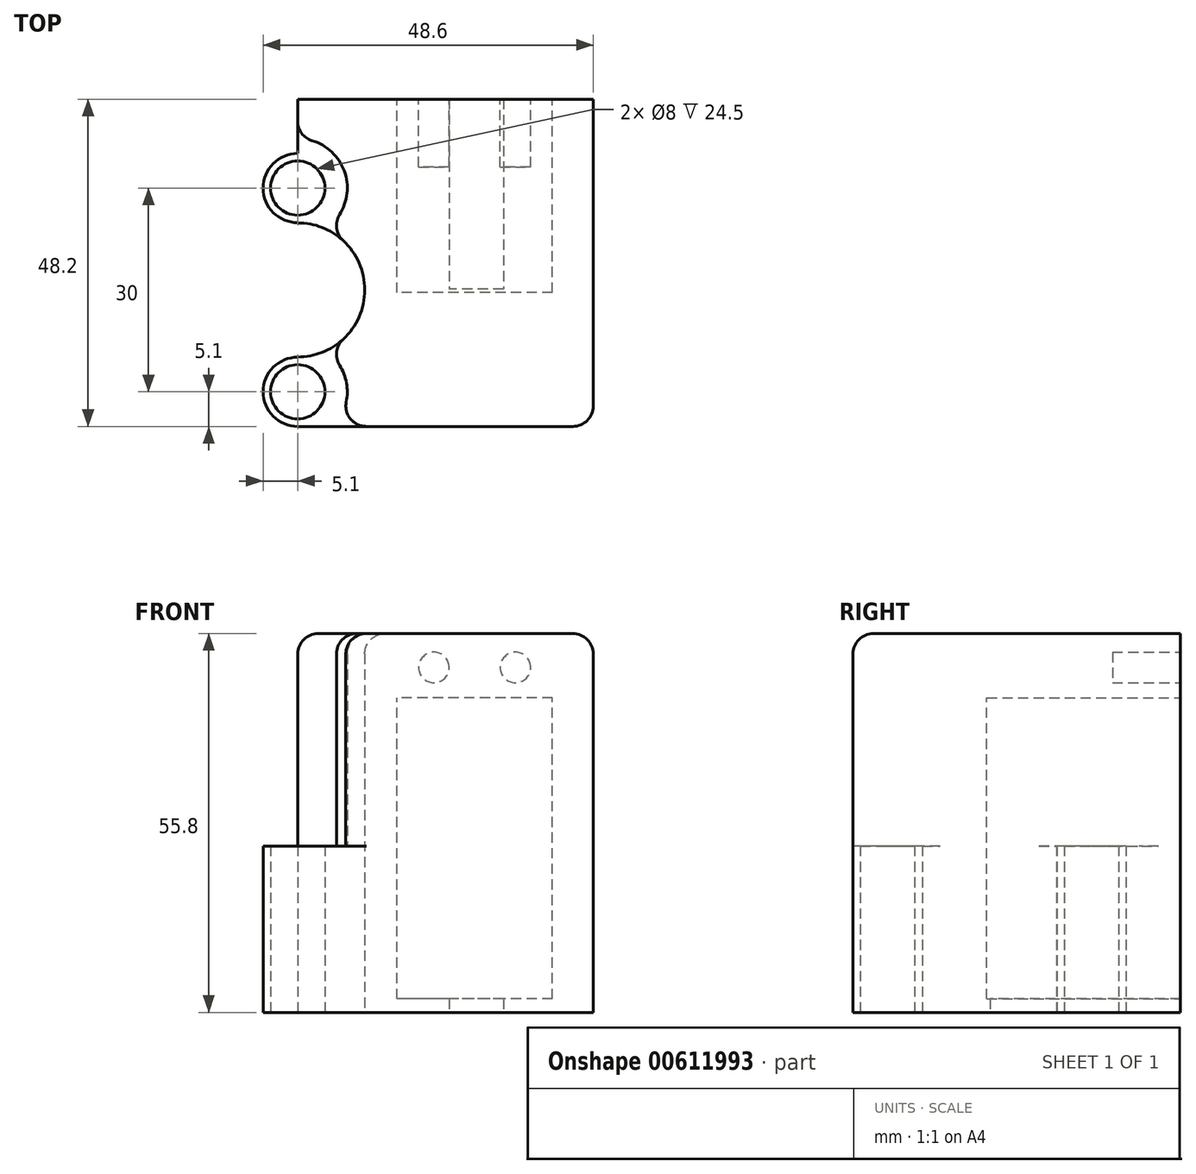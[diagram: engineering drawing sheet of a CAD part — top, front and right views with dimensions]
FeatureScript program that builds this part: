
annotation { "Feature Type Name" : "Feature", "Feature Type Description" : "" }
export const myFeature = defineFeature(function(context is Context, id is Id, definition is map)
    precondition{}
    {
        {
            assignVariable(context, id + "F0", {"name" : "bolt_length", "anyValue" : 24.5});
        }
        {
            assignVariable(context, id + "F1", {"name" : "servo_padding", "anyValue" : 6});
        }
        {
            assignVariable(context, id + "F2", {"name" : "servo_length", "anyValue" : 43.8});
        }
        {
            assignVariable(context, id + "F3", {"name" : "servo_height", "anyValue" : 28});
        }
        {
            assignVariable(context, id + "F4", {"name" : "servo_kerf", "anyValue" : .5});
        }
        {
            var Q0;
            Q0=qCreatedBy(makeId("Top.planeOp"),FACE);
            var sketch = newSketch(context, id + "F5", { "sketchPlane" : qUnion([Q0])});
            skLineSegment(sketch, "E0.bottom", {"start": v(8, -15) * mm, "end": v(-8, -15) * mm, "construction": true});
            skLineSegment(sketch, "E0.top", {"start": v(8, 15) * mm, "end": v(-8, 15) * mm, "construction": true});
            skLineSegment(sketch, "E0.left", {"start": v(8, -15) * mm, "end": v(8, 15) * mm, "construction": true});
            skLineSegment(sketch, "E0.right", {"start": v(-8, -15) * mm, "end": v(-8, 15) * mm, "construction": true});
            skPoint(sketch, "E0.middle", {"position": v(0, 0) * mm});
            skCircle(sketch, "E1", {"center": v(8, 15) * mm, "radius": 4 * mm});
            skCircle(sketch, "E2", {"center": v(8, -15) * mm, "radius": 4 * mm});
            skCircle(sketch, "E3", {"center": v(8, 15) * mm, "radius": 5.1 * mm});
            skCircle(sketch, "E4", {"center": v(8, -15) * mm, "radius": 5.1 * mm});
            skLineSegment(sketch, "E5.bottom", {"start": v(8, 15) * mm, "end": v(51.5, 15) * mm});
            skLineSegment(sketch, "E5.top", {"start": v(8, -15) * mm, "end": v(51.5, -15) * mm});
            skLineSegment(sketch, "E5.left", {"start": v(8, 15) * mm, "end": v(8, -15) * mm});
            skLineSegment(sketch, "E5.right", {"start": v(51.5, 15) * mm, "end": v(51.5, -15) * mm});
            skLineSegment(sketch, "E6.top", {"start": v(8, -20.1) * mm, "end": v(51.5, -20.1) * mm});
            skLineSegment(sketch, "E6.left", {"start": v(8, -15) * mm, "end": v(8, -20.1) * mm});
            skLineSegment(sketch, "E6.right", {"start": v(51.5, -15) * mm, "end": v(51.5, -20.1) * mm});
            skLineSegment(sketch, "E7.top", {"start": v(8, 20.1) * mm, "end": v(51.5, 20.1) * mm});
            skLineSegment(sketch, "E7.left", {"start": v(8, 15) * mm, "end": v(8, 20.1) * mm});
            skLineSegment(sketch, "E7.right", {"start": v(51.5, 15) * mm, "end": v(51.5, 20.1) * mm});
            skPoint(sketch, "E8.oppositeSnap0", {"position": v(51.5, 0) * mm});
            skLineSegment(sketch, "E8.top", {"start": v(8, 28.1) * mm, "end": v(51.5, 28.1) * mm});
            skLineSegment(sketch, "E8.left", {"start": v(8, 20.1) * mm, "end": v(8, 28.1) * mm});
            skLineSegment(sketch, "E8.right", {"start": v(51.5, 20.1) * mm, "end": v(51.5, 28.1) * mm});
            skCircle(sketch, "E9", {"center": v(8, -15) * mm, "radius": 7.3 * mm});
            skCircle(sketch, "E10", {"center": v(8, 15) * mm, "radius": 7.3 * mm});
            skLineSegment(sketch, "E11", {"start": v(8, 0) * mm, "end": v(8, 0) * mm});
            skCircle(sketch, "E12", {"center": v(8, 0) * mm, "radius": 9.88 * mm});
            skSolve(sketch);
        }
        {
            var Q0;
            {var subQ0=sQuery(id+"F5.wireOp",EDGE,"E7.left");var subQ1=sQuery(id+"F5.wireOp",EDGE,"E1");var subQ2=makeQuery(id+"F5.imprint","INTERSECT",VERTEX,{"derivedFrom":[subQ1,subQ0]});Q0=makeQuery(id+"F5.imprint","IMPRINT",FACE,{"disambiguationData":[TD([[makeQuery(id+"F5.imprint","IMPRINT",EDGE,{"disambiguationData":[TD([[subQ2,1.0]])],"derivedFrom":subQ1}),-1.0]])]});}
            var Q1;
            {var subQ0=sQuery(id+"F5.wireOp",EDGE,"E7.left");var subQ1=sQuery(id+"F5.wireOp",EDGE,"E1");var subQ2=makeQuery(id+"F5.imprint","INTERSECT",VERTEX,{"derivedFrom":[subQ1,subQ0]});Q1=makeQuery(id+"F5.imprint","IMPRINT",FACE,{"disambiguationData":[TD([[makeQuery(id+"F5.imprint","IMPRINT",EDGE,{"disambiguationData":[TD([[subQ2,-1.0]])],"derivedFrom":subQ1}),-1.0]])]});}
            var Q2;
            {var subQ0=sQuery(id+"F5.wireOp",EDGE,"E5.bottom");var subQ1=sQuery(id+"F5.wireOp",EDGE,"E1");var subQ2=makeQuery(id+"F5.imprint","INTERSECT",VERTEX,{"derivedFrom":[subQ1,subQ0]});Q2=makeQuery(id+"F5.imprint","IMPRINT",FACE,{"disambiguationData":[TD([[makeQuery(id+"F5.imprint","IMPRINT",EDGE,{"disambiguationData":[TD([[subQ2,1.0]])],"derivedFrom":subQ1}),-1.0]])]});}
            var Q3;
            {var subQ0=sQuery(id+"F5.wireOp",EDGE,"E5.left");var subQ1=sQuery(id+"F5.wireOp",EDGE,"E2");var subQ2=makeQuery(id+"F5.imprint","INTERSECT",VERTEX,{"derivedFrom":[subQ1,subQ0]});Q3=makeQuery(id+"F5.imprint","IMPRINT",FACE,{"disambiguationData":[TD([[makeQuery(id+"F5.imprint","IMPRINT",EDGE,{"disambiguationData":[TD([[subQ2,-1.0]])],"derivedFrom":subQ1}),-1.0]])]});}
            var Q4;
            {var subQ0=sQuery(id+"F5.wireOp",EDGE,"E5.left");var subQ1=sQuery(id+"F5.wireOp",EDGE,"E2");var subQ2=makeQuery(id+"F5.imprint","INTERSECT",VERTEX,{"derivedFrom":[subQ1,subQ0]});Q4=makeQuery(id+"F5.imprint","IMPRINT",FACE,{"disambiguationData":[TD([[makeQuery(id+"F5.imprint","IMPRINT",EDGE,{"disambiguationData":[TD([[subQ2,1.0]])],"derivedFrom":subQ1}),-1.0]])]});}
            var Q5;
            {var subQ0=sQuery(id+"F5.wireOp",EDGE,"E5.top");var subQ1=sQuery(id+"F5.wireOp",EDGE,"E2");var subQ2=makeQuery(id+"F5.imprint","INTERSECT",VERTEX,{"derivedFrom":[subQ1,subQ0]});Q5=makeQuery(id+"F5.imprint","IMPRINT",FACE,{"disambiguationData":[TD([[makeQuery(id+"F5.imprint","IMPRINT",EDGE,{"disambiguationData":[TD([[subQ2,1.0]])],"derivedFrom":subQ1}),-1.0]])]});}
            var Q6;
            {var subQ1=sQuery(id+"F5.wireOp",EDGE,"E4");var subQ3=sQuery(id+"F5.wireOp",EDGE,"E5.top");var subQ4=makeQuery(id+"F5.imprint","INTERSECT",VERTEX,{"derivedFrom":[subQ1,subQ3]});Q6=makeQuery(id+"F5.imprint","IMPRINT",FACE,{"disambiguationData":[TD([[makeQuery(id+"F5.imprint","IMPRINT",EDGE,{"disambiguationData":[TD([[subQ4,-1.0]])],"derivedFrom":subQ3}),-1.0]])]});}
            var Q7;
            {var subQ0=sQuery(id+"F5.wireOp",EDGE,"E6.right");Q7=makeQuery(id+"F5.imprint","IMPRINT",FACE,{"disambiguationData":[TD([[makeQuery(id+"F5.imprint","IMPRINT",EDGE,{"derivedFrom":subQ0}),-1.0]])]});}
            var Q8;
            {var subQ1=sQuery(id+"F5.wireOp",EDGE,"E5.right");Q8=makeQuery(id+"F5.imprint","IMPRINT",FACE,{"disambiguationData":[TD([[makeQuery(id+"F5.imprint","IMPRINT",EDGE,{"derivedFrom":subQ1}),-1.0]])]});}
            var Q9;
            {var subQ0=sQuery(id+"F5.wireOp",EDGE,"E5.left");var subQ1=sQuery(id+"F5.wireOp",EDGE,"E4");var subQ2=makeQuery(id+"F5.imprint","INTERSECT",VERTEX,{"derivedFrom":[subQ1,subQ0]});Q9=makeQuery(id+"F5.imprint","IMPRINT",FACE,{"disambiguationData":[TD([[makeQuery(id+"F5.imprint","IMPRINT",EDGE,{"disambiguationData":[TD([[subQ2,1.0]])],"derivedFrom":subQ1}),-1.0]])]});}
            var Q10;
            {var subQ0=sQuery(id+"F5.wireOp",EDGE,"E7.right");Q10=makeQuery(id+"F5.imprint","IMPRINT",FACE,{"disambiguationData":[TD([[makeQuery(id+"F5.imprint","IMPRINT",EDGE,{"derivedFrom":subQ0}),1.0]])]});}
            var Q11;
            {var subQ2=sQuery(id+"F5.wireOp",EDGE,"E8.top");Q11=makeQuery(id+"F5.imprint","IMPRINT",FACE,{"disambiguationData":[TD([[makeQuery(id+"F5.imprint","IMPRINT",EDGE,{"derivedFrom":subQ2}),-1.0]])]});}
            var Q12;
            {var subQ0=sQuery(id+"F5.wireOp",EDGE,"E5.bottom");var subQ1=sQuery(id+"F5.wireOp",EDGE,"E3");var subQ2=makeQuery(id+"F5.imprint","INTERSECT",VERTEX,{"derivedFrom":[subQ1,subQ0]});Q12=makeQuery(id+"F5.imprint","IMPRINT",FACE,{"disambiguationData":[TD([[makeQuery(id+"F5.imprint","IMPRINT",EDGE,{"disambiguationData":[TD([[subQ2,1.0]])],"derivedFrom":subQ1}),-1.0]])]});}
            var Q13;
            {var subQ0=sQuery(id+"F5.wireOp",EDGE,"E8.left");var subQ3=sQuery(id+"F5.wireOp",EDGE,"E10");var subQ5=makeQuery(id+"F5.imprint","INTERSECT",VERTEX,{"derivedFrom":[subQ0,subQ3]});Q13=makeQuery(id+"F5.imprint","IMPRINT",FACE,{"disambiguationData":[TD([[makeQuery(id+"F5.imprint","IMPRINT",EDGE,{"disambiguationData":[TD([[subQ5,1.0]])],"derivedFrom":subQ3}),1.0]])]});}
            var Q14;
            {var subQ1=sQuery(id+"F5.wireOp",EDGE,"E3");var subQ3=sQuery(id+"F5.wireOp",EDGE,"E5.bottom");var subQ4=makeQuery(id+"F5.imprint","INTERSECT",VERTEX,{"derivedFrom":[subQ1,subQ3]});Q14=makeQuery(id+"F5.imprint","IMPRINT",FACE,{"disambiguationData":[TD([[makeQuery(id+"F5.imprint","IMPRINT",EDGE,{"disambiguationData":[TD([[subQ4,-1.0]])],"derivedFrom":subQ3}),1.0]])]});}
            extrude(context, id + "F6", {"entities" : qUnion([Q0, Q1, Q2, Q3, Q4, Q5, Q6, Q7, Q8, Q9, Q10, Q11, Q12, Q13, Q14]), "depth" : (getVariable(context, 'bolt_length')) * mm, "offsetDistance" : 25 * mm});
        }
        {
            var Q0;
            {var subQ1=sQuery(id+"F5.wireOp",EDGE,"E5.right");Q0=makeQuery(id+"F5.imprint","IMPRINT",FACE,{"disambiguationData":[TD([[makeQuery(id+"F5.imprint","IMPRINT",EDGE,{"derivedFrom":subQ1}),-1.0]])]});}
            var Q1;
            {var subQ0=sQuery(id+"F5.wireOp",EDGE,"E6.right");Q1=makeQuery(id+"F5.imprint","IMPRINT",FACE,{"disambiguationData":[TD([[makeQuery(id+"F5.imprint","IMPRINT",EDGE,{"derivedFrom":subQ0}),-1.0]])]});}
            var Q2;
            {var subQ0=sQuery(id+"F5.wireOp",EDGE,"E7.right");Q2=makeQuery(id+"F5.imprint","IMPRINT",FACE,{"disambiguationData":[TD([[makeQuery(id+"F5.imprint","IMPRINT",EDGE,{"derivedFrom":subQ0}),1.0]])]});}
            var Q3;
            {var subQ2=sQuery(id+"F5.wireOp",EDGE,"E8.top");Q3=makeQuery(id+"F5.imprint","IMPRINT",FACE,{"disambiguationData":[TD([[makeQuery(id+"F5.imprint","IMPRINT",EDGE,{"derivedFrom":subQ2}),-1.0]])]});}
            extrude(context, id + "F7", {"entities" : qUnion([Q0, Q1, Q2, Q3]), "operationType" : NewBodyOperationType.ADD, "depth" : (getVariable(context, 'servo_length') + (getVariable(context, 'servo_padding') * 2)) * mm, "offsetDistance" : 25 * mm});
        }
        {
            var Q0;
            {var subQ0=sQuery(id+"F5.wireOp",EDGE,"E8.top");Q0=makeQuery(id+"F7.boolean.opBoolean","MERGE",FACE,{"derivedFrom":[makeQuery(id+"F6.opExtrude","SWEPT_FACE",FACE,{"disambiguationData":[OSD([subQ0])]}),makeQuery(id+"F7.opExtrude","SWEPT_FACE",FACE,{"disambiguationData":[OSD([subQ0])]})]});}
            var sketch = newSketch(context, id + "F8", { "sketchPlane" : qUnion([Q0])});
            skLineSegment(sketch, "E13.bottom", {"start": v(-51.5, 0) * mm, "end": v(-45.5, 0) * mm, "construction": true});
            skLineSegment(sketch, "E13.top", {"start": v(-51.5, 2) * mm, "end": v(-45.5, 2) * mm, "construction": true});
            skLineSegment(sketch, "E13.left", {"start": v(-51.5, 0) * mm, "end": v(-51.5, 2) * mm, "construction": true});
            skLineSegment(sketch, "E13.right", {"start": v(-45.5, 0) * mm, "end": v(-45.5, 2) * mm, "construction": true});
            skLineSegment(sketch, "E14.bottom", {"start": v(-45.5, 2) * mm, "end": v(-22.6, 2) * mm});
            skLineSegment(sketch, "E14.top", {"start": v(-45.5, 46.3) * mm, "end": v(-22.6, 46.3) * mm});
            skLineSegment(sketch, "E14.left", {"start": v(-45.5, 2) * mm, "end": v(-45.5, 46.3) * mm});
            skLineSegment(sketch, "E14.right", {"start": v(-22.6, 2) * mm, "end": v(-22.6, 46.3) * mm});
            skLineSegment(sketch, "E15.bottom", {"start": v(-28.05, 41.8) * mm, "end": v(-40.05, 41.8) * mm, "construction": true});
            skLineSegment(sketch, "E15.top", {"start": v(-28.05, 50.8) * mm, "end": v(-40.05, 50.8) * mm, "construction": true});
            skLineSegment(sketch, "E15.left", {"start": v(-28.05, 41.8) * mm, "end": v(-28.05, 50.8) * mm, "construction": true});
            skLineSegment(sketch, "E15.right", {"start": v(-40.05, 41.8) * mm, "end": v(-40.05, 50.8) * mm, "construction": true});
            skPoint(sketch, "E15.middle", {"position": v(-34.05, 46.3) * mm});
            skCircle(sketch, "E16", {"center": v(-40.05, 50.8) * mm, "radius": 2.25 * mm});
            skCircle(sketch, "E17", {"center": v(-28.05, 50.8) * mm, "radius": 2.25 * mm});
            skSolve(sketch);
        }
        {
            var Q0;
            Q0=makeQuery(id+"F8.imprint","IMPRINT",FACE,{"disambiguationData":[TD([[makeQuery(id+"F8.imprint","IMPRINT",EDGE,{"derivedFrom":sQuery(id+"F8.wireOp",EDGE,"E14.bottom")}),1.0]])]});
            extrude(context, id + "F9", {"entities" : qUnion([Q0]), "operationType" : NewBodyOperationType.REMOVE, "oppositeDirection" : true, "depth" : (getVariable(context, 'servo_height') + getVariable(context, 'servo_kerf')) * mm, "offsetDistance" : 25 * mm});
        }
        {
            var Q0;
            Q0=makeQuery(id+"F7.opExtrude","CAP_EDGE",EDGE,{"disambiguationData":[OSD([sQuery(id+"F5.wireOp",EDGE,"E10")])],"isStart":false});
            var Q1;
            {var subQ0=sQuery(id+"F5.wireOp",EDGE,"E5.left");Q1=makeQuery(id+"F7.opExtrude","CAP_EDGE",EDGE,{"disambiguationData":[OSD([subQ0]),TDD([makeQuery(id+"F5.imprint","IMPRINT",EDGE,{"disambiguationData":[TD([[makeQuery(id+"F5.imprint","INTERSECT",VERTEX,{"derivedFrom":[subQ0,sQuery(id+"F5.wireOp",EDGE,"E10")]}),-1.0]])],"derivedFrom":subQ0})])],"isStart":false});}
            var Q2;
            Q2=makeQuery(id+"F7.opExtrude","CAP_EDGE",EDGE,{"disambiguationData":[OSD([sQuery(id+"F5.wireOp",EDGE,"E12")])],"isStart":false});
            var Q3;
            {var subQ0=sQuery(id+"F5.wireOp",EDGE,"E5.left");Q3=makeQuery(id+"F7.opExtrude","CAP_EDGE",EDGE,{"disambiguationData":[OSD([subQ0]),TDD([makeQuery(id+"F5.imprint","IMPRINT",EDGE,{"disambiguationData":[TD([[makeQuery(id+"F5.imprint","INTERSECT",VERTEX,{"disambiguationData":[OD(1.0)],"derivedFrom":[subQ0,sQuery(id+"F5.wireOp",EDGE,"E12")]}),-1.0]])],"derivedFrom":subQ0})])],"isStart":false});}
            var Q4;
            Q4=makeQuery(id+"F7.opExtrude","CAP_EDGE",EDGE,{"disambiguationData":[OSD([sQuery(id+"F5.wireOp",EDGE,"E9")])],"isStart":false});
            var Q5;
            Q5=makeQuery(id+"F7.opExtrude","CAP_EDGE",EDGE,{"disambiguationData":[OSD([sQuery(id+"F5.wireOp",EDGE,"E6.top")])],"isStart":false});
            var Q6;
            {var subQ0=sQuery(id+"F5.wireOp",EDGE,"E6.right");var subQ1=sQuery(id+"F5.wireOp",EDGE,"E6.top");Q6=makeQuery(id+"F7.boolean.opBoolean","MERGE",EDGE,{"derivedFrom":[makeQuery(id+"F6.opExtrude","SWEPT_EDGE",EDGE,{"disambiguationData":[OSD([subQ1,subQ0])]}),makeQuery(id+"F7.opExtrude","SWEPT_EDGE",EDGE,{"disambiguationData":[OSD([subQ1,subQ0])]})]});}
            var Q7;
            Q7=makeQuery(id+"F7.opExtrude","CAP_EDGE",EDGE,{"disambiguationData":[OSD([sQuery(id+"F5.wireOp",EDGE,"E5.right"),sQuery(id+"F5.wireOp",EDGE,"E6.right"),sQuery(id+"F5.wireOp",EDGE,"E7.right"),sQuery(id+"F5.wireOp",EDGE,"E8.right")])],"isStart":false});
            var Q8;
            Q8=makeQuery(id+"F7.opExtrude","SWEPT_EDGE",EDGE,{"disambiguationData":[OSD([sQuery(id+"F5.wireOp",EDGE,"E6.top"),sQuery(id+"F5.wireOp",EDGE,"E9")])]});
            var Q9;
            Q9=makeQuery(id+"F7.opExtrude","SWEPT_EDGE",EDGE,{"disambiguationData":[OSD([sQuery(id+"F5.wireOp",EDGE,"E8.left"),sQuery(id+"F5.wireOp",EDGE,"E10")])]});
            var Q10;
            Q10=makeQuery(id+"F7.opExtrude","CAP_EDGE",EDGE,{"disambiguationData":[OSD([sQuery(id+"F5.wireOp",EDGE,"E8.left")])],"isStart":false});
            var Q11;
            Q11=makeQuery(id+"F7.opExtrude","SWEPT_EDGE",EDGE,{"disambiguationData":[OSD([sQuery(id+"F5.wireOp",EDGE,"E10"),sQuery(id+"F5.wireOp",EDGE,"E12")])]});
            var Q12;
            Q12=makeQuery(id+"F7.opExtrude","SWEPT_EDGE",EDGE,{"disambiguationData":[OSD([sQuery(id+"F5.wireOp",EDGE,"E9"),sQuery(id+"F5.wireOp",EDGE,"E12")])]});
            fillet(context, id + "F10", {"entities" : qUnion([Q0, Q1, Q2, Q3, Q4, Q5, Q6, Q7, Q8, Q9, Q10, Q11, Q12]), "radius" : 3 * mm, "tangentPropagation" : true, "allowEdgeOverflow" : false});
        }
        {
            var Q0;
            Q0=makeQuery(id+"F8.imprint","IMPRINT",FACE,{"disambiguationData":[TD([[makeQuery(id+"F8.imprint","IMPRINT",EDGE,{"derivedFrom":sQuery(id+"F8.wireOp",EDGE,"E17")}),1.0]])]});
            var Q1;
            Q1=makeQuery(id+"F8.imprint","IMPRINT",FACE,{"disambiguationData":[TD([[makeQuery(id+"F8.imprint","IMPRINT",EDGE,{"derivedFrom":sQuery(id+"F8.wireOp",EDGE,"E16")}),1.0]])]});
            extrude(context, id + "F11", {"entities" : qUnion([Q0, Q1]), "operationType" : NewBodyOperationType.REMOVE, "oppositeDirection" : true, "depth" : 10 * mm, "offsetDistance" : 25 * mm});
        }
        {
            var Q0;
            Q0=makeQuery(id+"F6.opExtrude","CAP_FACE",FACE,{"disambiguationData":[OSD([sQuery(id+"F5.wireOp",EDGE,"E1"),sQuery(id+"F5.wireOp",EDGE,"E2"),sQuery(id+"F5.wireOp",EDGE,"E3"),sQuery(id+"F5.wireOp",EDGE,"E4"),sQuery(id+"F5.wireOp",EDGE,"E5.left"),sQuery(id+"F5.wireOp",EDGE,"E5.right"),sQuery(id+"F5.wireOp",EDGE,"E6.top"),sQuery(id+"F5.wireOp",EDGE,"E6.right"),sQuery(id+"F5.wireOp",EDGE,"E7.right"),sQuery(id+"F5.wireOp",EDGE,"E8.top"),sQuery(id+"F5.wireOp",EDGE,"E8.left"),sQuery(id+"F5.wireOp",EDGE,"E8.right"),sQuery(id+"F5.wireOp",EDGE,"E12")])],"isStart":true});
            var sketch = newSketch(context, id + "F12", { "sketchPlane" : qUnion([Q0])});
            skLineSegment(sketch, "E18", {"start": v(51.5, -28.1) * mm, "end": v(34.3, -28.1) * mm, "construction": true});
            skLineSegment(sketch, "E19.bottom", {"start": v(38.3, -56.1) * mm, "end": v(30.3, -56.1) * mm});
            skLineSegment(sketch, "E19.top", {"start": v(38.3, -0.1) * mm, "end": v(30.3, -0.1) * mm});
            skLineSegment(sketch, "E19.left", {"start": v(38.3, -56.1) * mm, "end": v(38.3, -0.1) * mm});
            skLineSegment(sketch, "E19.right", {"start": v(30.3, -56.1) * mm, "end": v(30.3, -0.1) * mm});
            skPoint(sketch, "E19.middle", {"position": v(34.3, -28.1) * mm});
            skSolve(sketch);
        }
        {
            var Q0;
            {var subQ0=sQuery(id+"F12.wireOp",EDGE,"E19.top");Q0=makeQuery(id+"F12.imprint","IMPRINT",FACE,{"disambiguationData":[TD([[makeQuery(id+"F12.imprint","IMPRINT",EDGE,{"derivedFrom":subQ0}),1.0]])]});}
            extrude(context, id + "F13", {"entities" : qUnion([Q0]), "operationType" : NewBodyOperationType.REMOVE, "oppositeDirection" : true, "depth" : 25 * mm, "offsetDistance" : 25 * mm});
        }
    });
